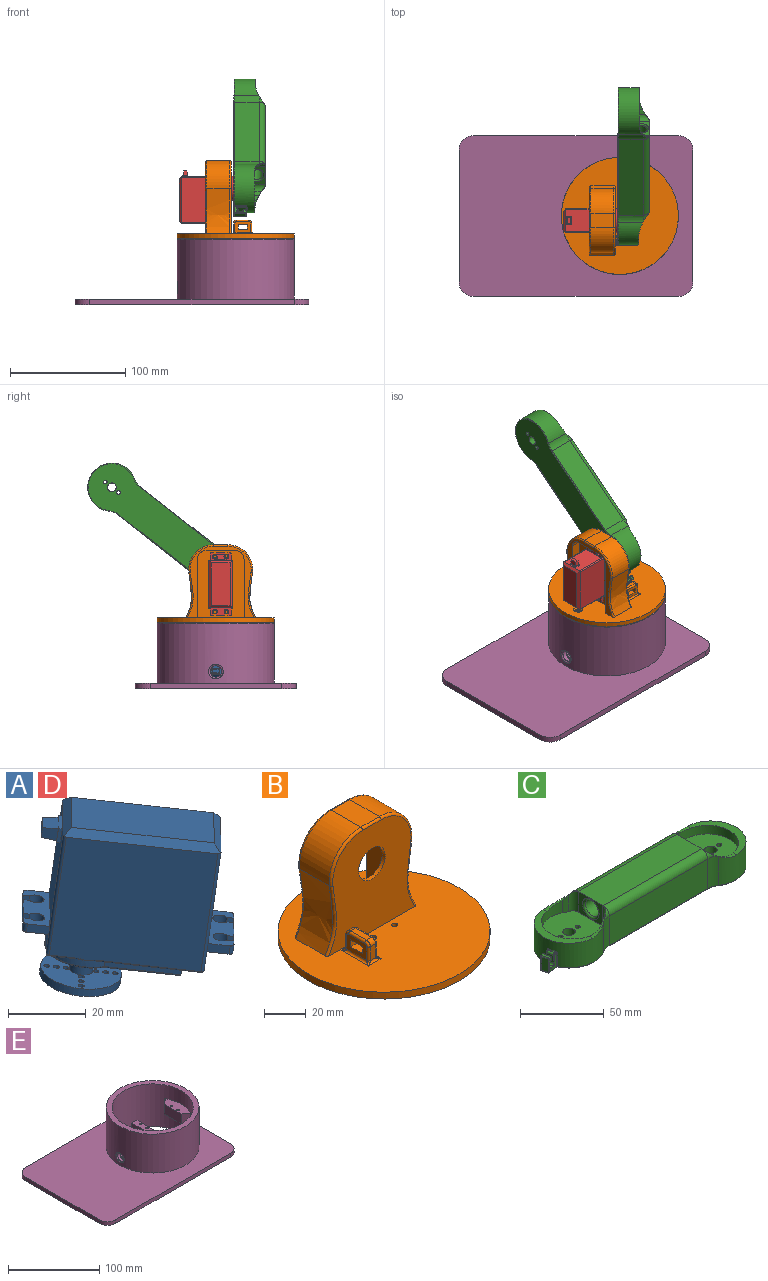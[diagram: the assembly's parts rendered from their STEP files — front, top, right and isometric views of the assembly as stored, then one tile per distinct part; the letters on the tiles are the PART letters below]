
ASSEMBLY  parts=5 mates=7
PART A: 116 faces, bbox 51.5x51x50.8 mm
  f0: cylinder r=0.75mm len=2.43mm, axis (-0.18,0,-0.98), area 10.4mm2, adj f111,f112
  f1: cylinder r=0.75mm len=2.43mm, axis (-0.18,0,-0.98), area 10.4mm2, adj f111,f112
  f2: cylinder r=0.75mm len=2.43mm, axis (-0.18,0,-0.98), area 10.4mm2, adj f111,f112
  f3: cylinder r=0.75mm len=2.43mm, axis (-0.18,0,-0.98), area 10.4mm2, adj f111,f112
  f4: cylinder r=0.75mm len=2.43mm, axis (-0.18,0,-0.98), area 10.4mm2, adj f111,f112
  f5: cylinder r=0.75mm len=2.43mm, axis (-0.18,0,-0.98), area 10.4mm2, adj f111,f112
  f6: cylinder r=0.75mm len=2.43mm, axis (-0.18,0,-0.98), area 10.4mm2, adj f111,f112
  f7: cylinder r=0.75mm len=2.43mm, axis (-0.18,0,-0.98), area 10.4mm2, adj f111,f112
  f8: cylinder r=0.75mm len=2.43mm, axis (-0.18,0,-0.98), area 10.4mm2, adj f111,f112
  f9: cylinder r=0.75mm len=2.43mm, axis (-0.18,0,-0.98), area 10.4mm2, adj f111,f112
  f10: cylinder r=0.75mm len=2.43mm, axis (-0.18,0,-0.98), area 10.4mm2, adj f111,f112
  f11: cylinder r=0.75mm len=2.43mm, axis (-0.18,0,-0.98), area 10.4mm2, adj f111,f112
  f12: cylinder r=10.5mm len=21.06mm, axis (0.18,0,0.98), area 145.1mm2, adj f111,f112
  f13: torus R=9.85mm, axis (-0.18,0,-0.98), area 26.7mm2, adj f21,f47,f82,f83
  f14: cylinder r=2.1mm len=4.56mm, axis (-0.18,0,-0.98), area 25.2mm2, adj f28,f29,f76,f77
  f15: cylinder r=2.1mm len=4.56mm, axis (-0.18,0,-0.98), area 25.2mm2, adj f27,f29,f74,f75
  f16: cylinder r=2.1mm len=4.56mm, axis (-0.18,0,-0.98), area 25.2mm2, adj f31,f33,f64,f65
  f17: cylinder r=2.1mm len=4.56mm, axis (-0.18,0,-0.98), area 25.2mm2, adj f32,f33,f62,f63
  f18: cylinder r=3mm len=6.62mm, axis (0.18,0,0.98), area 75.4mm2, adj f49,f111
  f19: cylinder r=5.35mm len=10.7mm, axis (0.18,0,0.98), area 20.2mm2, adj f48,f49
  f20: cylinder r=6.5mm len=13.02mm, axis (0.18,0,0.98), area 53.1mm2, adj f47,f48
  f21: cylinder r=10.25mm len=20.17mm, axis (0.18,0,0.98), area 81.6mm2, adj f13,f37,f38,f39,f45,f46,f85,f87
  f22: plane 5.62x5.02mm, normal (-0.7,0.71,0.13), area 7.3mm2, adj f102,f103,f104,f105,f106,f107,f108,f109
  f23: plane 36.52x19.42mm, normal (-0.7,0.71,0.13), area 579.5mm2, adj f31,f32,f33,f54,f55,f56,f59,f60
  f24: plane 5.65x5.3mm, normal (0.7,-0.71,-0.13), area 18mm2, adj f27,f28,f29,f74,f77,f80
  f25: plane 5x4.81mm, normal (0.7,0.71,-0.13), area 5.1mm2, adj f27,f40,f80
  f26: plane 5x4.81mm, normal (-0.7,-0.71,0.13), area 5.1mm2, adj f28,f40,f80
  f27: plane 11x10.41mm, normal (-0.18,0,-0.98), area 42.1mm2, adj f15,f24,f25,f40,f72,f73,f74,f75
  f28: plane 10.82x10.58mm, normal (-0.18,0,-0.98), area 42.1mm2, adj f14,f24,f26,f30,f40,f71,f76,f77
  f29: plane 17.48x17.19mm, normal (0.18,0,0.98), area 91mm2, adj f14,f15,f24,f30,f40,f71,f72,f73
  f30: plane 2.61x1.82mm, normal (0.7,-0.71,-0.13), area 4.8mm2, adj f28,f29,f76,f79
  f31: plane 11x10.41mm, normal (-0.18,0,-0.98), area 42.1mm2, adj f16,f23,f34,f59,f61,f64,f65,f67
  f32: plane 10.82x10.58mm, normal (-0.18,0,-0.98), area 42.1mm2, adj f17,f23,f34,f35,f60,f62,f63,f66
  f33: plane 17.48x17.19mm, normal (0.18,0,0.98), area 91mm2, adj f16,f17,f23,f34,f35,f59,f60,f61
  f34: plane 5.65x5.3mm, normal (-0.7,0.71,0.13), area 18mm2, adj f31,f32,f33,f63,f64,f70
  f35: plane 2.61x1.82mm, normal (-0.7,0.71,0.13), area 4.8mm2, adj f32,f33,f62,f66
  f36: cylinder r=3.32mm len=4.53mm, axis (0.18,0,0.98), area 9.6mm2, adj f37,f44,f81
  f37: plane 33.22x32.68mm, normal (-0.18,0,-0.98), area 137.4mm2, adj f21,f36,f44,f45,f46,f86,f88,f89
  f38: plane 9.76x4.79mm, normal (-0.18,0,-0.98), area 16mm2, adj f21,f93,f94,f96
  f39: plane 9.92x4.72mm, normal (-0.18,0,-0.98), area 16mm2, adj f21,f98,f99,f101
  f40: plane 36.43x19.34mm, normal (0.7,-0.71,-0.13), area 608mm2, adj f25,f26,f27,f28,f29,f51,f57,f58
  f41: plane 39.21x33.78mm, normal (-0.7,-0.71,0.13), area 1364.1mm2, adj f52,f55,f57,f85,f86,f97,f98
  f42: plane 39.11x33.68mm, normal (0.7,0.71,-0.13), area 1364.1mm2, adj f53,f56,f58,f87,f89,f95,f96
  f43: plane 37.83x37.22mm, normal (0.18,0,0.98), area 610.5mm2, adj f51,f52,f53,f54
  f44: plane 12.79x12.65mm, normal (0.7,-0.71,-0.13), area 23.7mm2, adj f36,f37,f45,f46,f50,f81,f84
  f45: plane 14.2x14.09mm, normal (-0.7,-0.71,0.13), area 37.9mm2, adj f21,f37,f44,f83
  f46: plane 14.2x14.09mm, normal (0.7,0.71,-0.13), area 37.9mm2, adj f21,f37,f44,f82
  f47: plane 33.27x32.74mm, normal (-0.18,0,-0.98), area 446.8mm2, adj f13,f20,f82,f83,f84
  f48: plane 13x12.79mm, normal (-0.18,0,-0.98), area 42.8mm2, adj f19,f20
  f49: plane 10.7x10.53mm, normal (-0.18,0,-0.98), area 61.6mm2, adj f18,f19
  f50: plane 3.65x3.59mm, normal (-0.18,0,-0.98), area 5.1mm2, adj f44,f81
  f51: plane 14.28x14.05mm, normal (0.62,-0.5,0.61), area 52.1mm2, adj f40,f43,f52,f53,f57,f58
  f52: plane 28.77x28.63mm, normal (-0.37,-0.5,0.79), area 110.1mm2, adj f41,f43,f51,f54,f55,f57
  f53: plane 28.77x28.31mm, normal (0.62,0.5,0.61), area 110.1mm2, adj f42,f43,f51,f54,f56,f58
  f54: plane 14.37x14.28mm, normal (-0.37,0.5,0.79), area 52.1mm2, adj f23,f43,f52,f53,f55,f56
  f55: cylinder r=0.8mm len=34.32mm, axis (0.18,0,0.98), area 43.6mm2, adj f23,f41,f52,f54,f99
  f56: cylinder r=0.8mm len=34.48mm, axis (0.18,0,0.98), area 43.6mm2, adj f23,f42,f53,f54,f94
  f57: cylinder r=0.8mm len=34.48mm, axis (0.18,0,0.98), area 43.6mm2, adj f40,f41,f51,f52,f88
  f58: cylinder r=0.8mm len=34.32mm, axis (0.18,0,0.98), area 43.6mm2, adj f40,f42,f51,f53,f91
  f59: plane 4.46x4.1mm, normal (-0.7,-0.71,0.13), area 13.9mm2, adj f23,f31,f33,f67
  f60: plane 4.46x4.1mm, normal (0.7,0.71,-0.13), area 13.9mm2, adj f23,f32,f33,f66
  f61: plane 2.61x1.82mm, normal (-0.7,0.71,0.13), area 4.8mm2, adj f31,f33,f65,f67
  f62: plane 2.57x1.55mm, normal (-0.7,-0.71,0.13), area 3.9mm2, adj f17,f32,f33,f35
  f63: plane 2.57x1.55mm, normal (0.7,0.71,-0.13), area 3.9mm2, adj f17,f32,f33,f34
  f64: plane 2.57x1.55mm, normal (-0.7,-0.71,0.13), area 3.9mm2, adj f16,f31,f33,f34
  f65: plane 2.57x1.55mm, normal (0.7,0.71,-0.13), area 3.9mm2, adj f16,f31,f33,f61
  f66: cylinder r=1mm len=2.61mm, axis (0.18,0,0.98), area 3.8mm2, adj f32,f33,f35,f60
  f67: cylinder r=1mm len=2.41mm, axis (-0.18,0,-0.98), area 3.8mm2, adj f31,f33,f59,f61
  f68: plane 4.81x4.73mm, normal (-0.7,-0.71,0.13), area 5.1mm2, adj f23,f31,f70
  f69: plane 4.81x4.73mm, normal (0.7,0.71,-0.13), area 5.1mm2, adj f23,f32,f70
  f70: plane 5.52x5.16mm, normal (-0.32,0.15,-0.93), area 7mm2, adj f23,f34,f68,f69
  f71: plane 4.46x4.1mm, normal (-0.7,-0.71,0.13), area 13.9mm2, adj f28,f29,f40,f79
  f72: plane 4.46x4.1mm, normal (0.7,0.71,-0.13), area 13.9mm2, adj f27,f29,f40,f78
  f73: plane 2.61x1.82mm, normal (0.7,-0.71,-0.13), area 4.8mm2, adj f27,f29,f75,f78
  f74: plane 2.57x1.55mm, normal (0.7,0.71,-0.13), area 3.9mm2, adj f15,f24,f27,f29
  f75: plane 2.57x1.55mm, normal (-0.7,-0.71,0.13), area 3.9mm2, adj f15,f27,f29,f73
  f76: plane 2.57x1.55mm, normal (0.7,0.71,-0.13), area 3.9mm2, adj f14,f28,f29,f30
  f77: plane 2.57x1.55mm, normal (-0.7,-0.71,0.13), area 3.9mm2, adj f14,f24,f28,f29
  f78: cylinder r=1mm len=2.41mm, axis (-0.18,0,-0.98), area 3.8mm2, adj f27,f29,f72,f73
  f79: cylinder r=1mm len=2.61mm, axis (0.18,0,0.98), area 3.8mm2, adj f28,f29,f30,f71
  f80: plane 5.69x5.52mm, normal (-0.02,-0.15,-0.99), area 7mm2, adj f24,f25,f26,f40
  f81: torus R=2.92mm, axis (-0.18,0,-0.98), area 4.3mm2, adj f36,f44,f50
  f82: cylinder r=0.4mm len=14.45mm, axis (-0.7,0.71,0.13), area 12.4mm2, adj f13,f46,f47,f84
  f83: cylinder r=0.4mm len=14.45mm, axis (0.7,-0.71,-0.13), area 12.4mm2, adj f13,f45,f47,f84
  f84: cylinder r=0.4mm len=12.83mm, axis (0.7,0.71,-0.13), area 10.9mm2, adj f44,f47,f82,f83
  f85: bspline ~2.25x2.01mm, area 0.6mm2, adj f21,f41,f86
  f86: cylinder r=0.4mm len=19.46mm, axis (-0.7,0.71,0.13), area 17mm2, adj f37,f41,f85,f88
  f87: bspline ~2.29x2.04mm, area 0.6mm2, adj f21,f42,f89
  f88: torus R=0.4mm, axis (0.18,0,0.98), area 0.6mm2, adj f37,f57,f86,f90
  f89: cylinder r=0.4mm len=19.46mm, axis (0.7,-0.71,-0.13), area 17mm2, adj f37,f42,f87,f91
  f90: cylinder r=0.4mm len=13.65mm, axis (-0.7,-0.71,0.13), area 11.9mm2, adj f37,f40,f88,f91
  f91: torus R=0.4mm, axis (0.18,0,0.98), area 0.6mm2, adj f37,f58,f89,f90
  f92: bspline ~2.25x2.01mm, area 0.6mm2, adj f21,f23,f93
  f93: cylinder r=0.4mm len=4.96mm, axis (0.7,0.71,-0.13), area 4.2mm2, adj f23,f38,f92,f94
  f94: torus R=0.4mm, axis (0.18,0,0.98), area 0.6mm2, adj f38,f56,f93,f96
  f95: bspline ~2.25x2.01mm, area 0.6mm2, adj f21,f42,f96
  f96: cylinder r=0.4mm len=4.96mm, axis (0.7,-0.71,-0.13), area 4.2mm2, adj f38,f42,f94,f95
  f97: bspline ~2.29x1.97mm, area 0.6mm2, adj f21,f41,f98
  f98: cylinder r=0.4mm len=4.96mm, axis (-0.7,0.71,0.13), area 4.2mm2, adj f39,f41,f97,f99
  f99: torus R=0.4mm, axis (0.18,0,0.98), area 0.6mm2, adj f39,f55,f98,f101
  f100: bspline ~2.29x1.97mm, area 0.6mm2, adj f21,f23,f101
  f101: cylinder r=0.4mm len=4.96mm, axis (0.7,0.71,-0.13), area 4.2mm2, adj f23,f39,f99,f100
  f102: plane 4.26x1.45mm, normal (0.7,0.71,-0.13), area 4.2mm2, adj f22,f23,f103,f105
  f103: plane 5.66x5.57mm, normal (-0.18,0,-0.98), area 7mm2, adj f22,f23,f102,f104
  f104: plane 4.26x1.45mm, normal (-0.7,-0.71,0.13), area 4.2mm2, adj f22,f23,f103,f105
  f105: plane 5.66x5.57mm, normal (0.18,0,0.98), area 7mm2, adj f22,f23,f102,f104
  f106: plane 3.65x3.59mm, normal (0.63,0.77,-0.11), area 12.6mm2, adj f22,f107,f109,f110
  f107: plane 7.04x6.86mm, normal (-0.24,0.06,-0.97), area 23.9mm2, adj f22,f106,f108,f110
  f108: plane 3.56x3.1mm, normal (-0.75,-0.64,0.14), area 12.6mm2, adj f22,f107,f109,f110
  f109: plane 7.04x6.99mm, normal (0.12,0.06,0.99), area 23.9mm2, adj f22,f106,f108,f110
  f110: plane 4.4x3.96mm, normal (-0.7,0.71,0.13), area 15.7mm2, adj f106,f107,f108,f109
  f111: plane 21x20.66mm, normal (0.18,0,0.98), area 296.9mm2, adj f0,f1,f2,f3,f4,f5,f6,f7
  f112: plane 21x20.66mm, normal (-0.18,0,-0.98), area 325.2mm2, adj f0,f1,f2,f3,f4,f5,f6,f7
  f113: cylinder r=1.25mm len=4.38mm, axis (-0.18,0,-0.98), area 31.4mm2, adj f114,f115
  f114: plane 2.5x2.46mm, normal (-0.18,0,-0.98), area 4.9mm2, adj f113
  f115: plane 2.5x2.46mm, normal (0.18,0,0.98), area 4.9mm2, adj f113
PART B: 76 faces, bbox 101.9x101.9x69.5 mm
  f0: plane 13.46x9.46mm, normal (1,0,0), area 94.6mm2, adj f44,f45,f46,f47,f49,f63,f64,f65
  f1: plane 13.46x9.46mm, normal (-1,0,0), area 94.6mm2, adj f44,f45,f46,f47,f50,f70,f71,f72
  f2: plane 62.24x57.86mm, normal (0,1,0), area 673.2mm2, adj f6,f13,f14,f15,f16,f17,f57,f58
  f3: plane 62.24x57.86mm, normal (0,-1,0), area 2768mm2, adj f6,f23,f52,f53,f54,f55,f56
  f4: plane 19.96x12.41mm, normal (0,0,1), area 247.6mm2, adj f34,f35,f54,f60
  f5: plane 58.42x40.64mm, normal (0,1,0), area 1458.6mm2, adj f6,f13,f14,f15,f16,f17,f18,f19
  f6: plane 101.86x101.86mm, normal (0,0,1), area 6871.9mm2, adj f2,f3,f5,f8,f11,f12,f13,f17
  f7: plane 101.6x101.6mm, normal (0,0,-1), area 8004.4mm2, adj f8,f9,f11,f12,f38
  f8: cylinder r=50.8mm len=101.6mm, axis (0,0,-1), area 1276.7mm2, adj f6,f7
  f9: cylinder r=3.75mm len=7.5mm, axis (0,0,-1), area 35.3mm2, adj f7,f10
  f10: plane 7.5x7.5mm, normal (0,0,-1), area 44.2mm2, adj f9
  f11: cylinder r=1.5mm len=4mm, axis (0,0,-1), area 37.7mm2, adj f6,f7
  f12: cylinder r=1.5mm len=4mm, axis (0,0,-1), area 37.7mm2, adj f6,f7
  f13: plane 50.8x8.5mm, normal (1,0,0), area 431.8mm2, adj f2,f5,f6,f14
  f14: cylinder r=7.62mm len=8.5mm, axis (0,1,0), area 101.7mm2, adj f2,f5,f13,f15
  f15: plane 25.4x8.5mm, normal (0,0,-1), area 215.9mm2, adj f2,f5,f14,f16
  f16: cylinder r=7.62mm len=8.5mm, axis (0,1,0), area 101.7mm2, adj f2,f5,f15,f17
  f17: plane 50.8x8.5mm, normal (-1,0,0), area 431.8mm2, adj f2,f5,f6,f16
  f18: plane 21x12mm, normal (0,0,1), area 252mm2, adj f5,f19,f21,f22
  f19: plane 41.4x12mm, normal (1,0,0), area 496.8mm2, adj f5,f18,f20,f22
  f20: plane 21x12mm, normal (0,0,-1), area 252mm2, adj f5,f19,f21,f22
  f21: plane 41.4x12mm, normal (-1,0,0), area 496.8mm2, adj f5,f18,f20,f22
  f22: plane 41.4x21mm, normal (0,1,0), area 615mm2, adj f18,f19,f20,f21,f23
  f23: cylinder r=9mm len=18mm, axis (0,1,0), area 113.1mm2, adj f3,f22
  f24: cylinder r=1.3mm len=7.5mm, axis (0,1,0), area 61.3mm2, adj f5,f25
  f25: plane 2.6x2.6mm, normal (0,1,0), area 5.3mm2, adj f24
  f26: cylinder r=1.3mm len=7.5mm, axis (0,1,0), area 61.3mm2, adj f5,f27
  f27: plane 2.6x2.6mm, normal (0,1,0), area 5.3mm2, adj f26
  f28: cylinder r=1.3mm len=7.5mm, axis (0,1,0), area 61.3mm2, adj f5,f29
  f29: plane 2.6x2.6mm, normal (0,1,0), area 5.3mm2, adj f28
  f30: cylinder r=1.3mm len=7.5mm, axis (0,1,0), area 61.3mm2, adj f5,f31
  f31: plane 2.6x2.6mm, normal (0,1,0), area 5.3mm2, adj f30
  f32: extruded ~39.77x19.96mm, area 815.7mm2, adj f6,f35,f52,f57
  f33: extruded ~39.77x19.96mm, area 815.7mm2, adj f6,f34,f55,f59
  f34: cylinder r=21.59mm len=23.74mm, axis (0,1,0), area 719.8mm2, adj f4,f33,f56,f61
  f35: cylinder r=21.59mm len=23.74mm, axis (0,1,0), area 719.8mm2, adj f4,f32,f53,f58
  f36: cylinder r=2.5mm len=5mm, axis (0,0,1), area 22.9mm2, adj f37,f38
  f37: torus R=3.77mm, axis (0,0,1), area 37.1mm2, adj f6,f36
  f38: torus R=3.77mm, axis (0,0,1), area 37.1mm2, adj f7,f36
  f39: plane 8.19x3.46mm, normal (0,-1,0), area 28.3mm2, adj f43,f48,f67,f70
  f40: plane 8.19x3.46mm, normal (0,1,0), area 28.3mm2, adj f42,f51,f63,f74
  f41: plane 10.92x3.46mm, normal (0,0,1), area 37.8mm2, adj f42,f43,f65,f72
  f42: cylinder r=2.54mm len=3.46mm, axis (1,0,0), area 13.8mm2, adj f40,f41,f64,f73
  f43: cylinder r=2.54mm len=3.46mm, axis (-1,0,0), area 13.8mm2, adj f39,f41,f66,f71
  f44: plane 8x6mm, normal (0,0,1), area 48mm2, adj f0,f1,f45,f47
  f45: plane 6x4mm, normal (0,-1,0), area 24mm2, adj f0,f1,f44,f46
  f46: plane 8x6mm, normal (0,0,-1), area 48mm2, adj f0,f1,f45,f47
  f47: plane 6x4mm, normal (0,1,0), area 24mm2, adj f0,f1,f44,f46
  f48: cylinder r=1.27mm len=8.54mm, axis (1,0,0), area 12mm2, adj f6,f39,f68,f69
  f49: cylinder r=1.27mm len=18.54mm, axis (0,1,0), area 31.9mm2, adj f0,f6,f62,f68
  f50: cylinder r=1.27mm len=18.54mm, axis (0,-1,0), area 31.9mm2, adj f1,f6,f69,f75
  f51: cylinder r=1.27mm len=8.54mm, axis (-1,0,0), area 12mm2, adj f6,f40,f62,f75
  f52: bspline ~44.89x7.82mm, area 81.4mm2, adj f3,f6,f32,f53
  f53: torus R=20.32mm, axis (0,1,0), area 70.4mm2, adj f3,f35,f52,f54
  f54: cylinder r=1.27mm len=12.41mm, axis (-1,0,0), area 24.7mm2, adj f3,f4,f53,f56
  f55: bspline ~44.89x7.82mm, area 81.4mm2, adj f3,f6,f33,f56
  f56: torus R=20.32mm, axis (0,1,0), area 70.4mm2, adj f3,f34,f54,f55
  f57: bspline ~44.89x7.82mm, area 81.4mm2, adj f2,f6,f32,f58
  f58: torus R=20.32mm, axis (0,1,0), area 70.4mm2, adj f2,f35,f57,f60
  f59: bspline ~44.89x7.82mm, area 81.4mm2, adj f2,f6,f33,f61
  f60: cylinder r=1.27mm len=12.41mm, axis (1,0,0), area 24.7mm2, adj f2,f4,f58,f61
  f61: torus R=20.32mm, axis (0,1,0), area 70.4mm2, adj f2,f34,f59,f60
  f62: bspline ~2.54x2.54mm, area 1.7mm2, adj f49,f51,f63
  f63: cylinder r=1.27mm len=8.19mm, axis (0,0,-1), area 16.3mm2, adj f0,f40,f62,f64
  f64: torus R=1.27mm, axis (-1,0,0), area 6.5mm2, adj f0,f42,f63,f65
  f65: cylinder r=1.27mm len=10.92mm, axis (0,-1,0), area 21.8mm2, adj f0,f41,f64,f66
  f66: torus R=1.27mm, axis (-1,0,0), area 6.5mm2, adj f0,f43,f65,f67
  f67: cylinder r=1.27mm len=8.19mm, axis (0,0,1), area 16.3mm2, adj f0,f39,f66,f68
  f68: bspline ~2.54x2.54mm, area 1.7mm2, adj f48,f49,f67
  f69: bspline ~2.54x2.54mm, area 1.7mm2, adj f48,f50,f70
  f70: cylinder r=1.27mm len=8.19mm, axis (0,0,-1), area 16.3mm2, adj f1,f39,f69,f71
  f71: torus R=1.27mm, axis (-1,0,0), area 6.5mm2, adj f1,f43,f70,f72
  f72: cylinder r=1.27mm len=10.92mm, axis (0,1,0), area 21.8mm2, adj f1,f41,f71,f73
  f73: torus R=1.27mm, axis (-1,0,0), area 6.5mm2, adj f1,f42,f72,f74
  f74: cylinder r=1.27mm len=8.19mm, axis (0,0,1), area 16.3mm2, adj f1,f40,f73,f75
  f75: bspline ~2.54x2.54mm, area 1.7mm2, adj f50,f51,f74
PART C: 113 faces, bbox 171.4x45.5x28.2 mm
  f0: plane 9.98x6.97mm, normal (-0.19,0.98,0), area 32.9mm2, adj f62,f65,f66,f69,f70,f73,f74,f77
  f1: plane 4.91x1.58mm, normal (0,0,1), area 1.7mm2, adj f55,f89,f90,f91
  f2: cylinder r=21mm len=42mm, axis (0,0,-1), area 1562mm2, adj f6,f12,f30,f31,f32,f90,f95,f96
  f3: plane 37.08x33.94mm, normal (0,0,1), area 987.5mm2, adj f4,f16,f17,f18,f27,f28,f29,f43
  f4: plane 20.33x15.24mm, normal (-1,0,0), area 156.6mm2, adj f3,f21,f43,f44,f45
  f5: plane 37.08x34.02mm, normal (0,0,1), area 989.7mm2, adj f13,f14,f15,f20,f23,f24,f25,f41
  f6: cylinder r=12.7mm len=21.65mm, axis (0,0,-1), area 158.1mm2, adj f2,f7,f31,f35,f106
  f7: plane 83.29x21.65mm, normal (0,-1,0), area 1803.4mm2, adj f6,f8,f36,f108
  f8: cylinder r=12.7mm len=21.65mm, axis (0,0,-1), area 158.1mm2, adj f7,f9,f33,f37,f110
  f9: cylinder r=21mm len=42mm, axis (0,0,-1), area 1637.3mm2, adj f8,f10,f26,f33,f34,f112
  f10: cylinder r=12.7mm len=21.65mm, axis (0,0,-1), area 158.1mm2, adj f9,f11,f34,f40,f111
  f11: plane 83.29x21.65mm, normal (0,1,0), area 1803.4mm2, adj f10,f12,f39,f109
  f12: cylinder r=12.7mm len=21.65mm, axis (0,0,-1), area 158.1mm2, adj f2,f11,f32,f38,f107
  f13: cylinder r=3.75mm len=12mm, axis (0,0,-1), area 282.7mm2, adj f5,f19
  f14: cylinder r=1.5mm len=12mm, axis (0,0,-1), area 113.1mm2, adj f5,f19
  f15: cylinder r=1.5mm len=12mm, axis (0,0,-1), area 113.1mm2, adj f5,f19
  f16: cylinder r=3.75mm len=12mm, axis (0,0,-1), area 282.7mm2, adj f3,f19
  f17: cylinder r=1.5mm len=12mm, axis (0,0,-1), area 113.1mm2, adj f3,f19
  f18: cylinder r=1.5mm len=12mm, axis (0,0,-1), area 113.1mm2, adj f3,f19
  f19: plane 168.64x40.98mm, normal (0,0,-1), area 5070.5mm2, adj f13,f14,f15,f16,f17,f18,f93,f98
  f20: plane 20.31x15.24mm, normal (1,0,0), area 156.2mm2, adj f5,f21,f41,f42,f46
  f21: plane 83.29x20.97mm, normal (0,0,1), area 1746.1mm2, adj f4,f20,f31,f32,f33,f34,f36,f39
  f22: cylinder r=5.71mm len=80.75mm, axis (1,0,0), area 2899.6mm2, adj f45,f46
  f23: cylinder r=13.72mm len=11.7mm, axis (0,0,-1), area 43.1mm2, adj f5,f24,f34,f41
  f24: cylinder r=18.54mm len=37.08mm, axis (0,0,-1), area 498.6mm2, adj f5,f23,f25,f26,f33,f34
  f25: cylinder r=13.72mm len=11.68mm, axis (0,0,-1), area 42.5mm2, adj f5,f24,f33,f42
  f26: plane 41.96x20.05mm, normal (0,0,1), area 253.9mm2, adj f9,f24,f33,f34
  f27: cylinder r=13.72mm len=11.7mm, axis (0,0,-1), area 43.1mm2, adj f3,f28,f31,f44
  f28: cylinder r=18.54mm len=37.08mm, axis (0,0,-1), area 497.5mm2, adj f3,f27,f29,f30,f31,f32
  f29: cylinder r=13.72mm len=11.7mm, axis (0,0,-1), area 43.1mm2, adj f3,f28,f32,f43
  f30: plane 41.96x20.05mm, normal (0,0,1), area 256.6mm2, adj f2,f28,f31,f32
  f31: cylinder r=25.4mm len=19.3mm, axis (0,-1,0), area 31.9mm2, adj f2,f6,f21,f27,f28,f30,f35,f44
  f32: cylinder r=25.4mm len=19.3mm, axis (0,-1,0), area 31.9mm2, adj f2,f12,f21,f28,f29,f30,f38,f43
  f33: cylinder r=25.4mm len=19.3mm, axis (0,-1,0), area 32.8mm2, adj f8,f9,f21,f24,f25,f26,f37,f42
  f34: cylinder r=25.4mm len=19.3mm, axis (0,-1,0), area 31.6mm2, adj f9,f10,f21,f23,f24,f26,f40,f41
  f35: torus R=17.78mm, axis (0,0,1), area 15.4mm2, adj f6,f31,f36
  f36: cylinder r=5.08mm len=83.29mm, axis (-1,0,0), area 664.6mm2, adj f7,f21,f35,f37
  f37: torus R=17.78mm, axis (0,0,1), area 15.4mm2, adj f8,f33,f36
  f38: torus R=17.78mm, axis (0,0,1), area 15.4mm2, adj f12,f32,f39
  f39: cylinder r=5.08mm len=83.29mm, axis (1,0,0), area 664.6mm2, adj f11,f21,f38,f40
  f40: torus R=17.78mm, axis (0,0,1), area 15.4mm2, adj f10,f34,f39
  f41: cylinder r=5.08mm len=15.24mm, axis (0,0,-1), area 91.5mm2, adj f5,f20,f23,f34
  f42: cylinder r=5.08mm len=15.24mm, axis (0,0,-1), area 91.9mm2, adj f5,f20,f25,f33
  f43: cylinder r=5.08mm len=15.24mm, axis (0,0,-1), area 91.5mm2, adj f3,f4,f29,f32
  f44: cylinder r=5.08mm len=15.24mm, axis (0,0,-1), area 91.5mm2, adj f3,f4,f27,f31
  f45: torus R=6.99mm, axis (1,0,0), area 77.4mm2, adj f4,f22
  f46: torus R=6.99mm, axis (1,0,0), area 77.4mm2, adj f20,f22
  f47: plane 9.98x7.13mm, normal (0.19,-0.98,0), area 34.5mm2, adj f61,f63,f64,f67,f68,f71,f72,f75
  f48: plane 9.98x4.79mm, normal (-0.96,-0.27,0), area 49.7mm2, adj f83,f88,f92,f93
  f49: plane 5.18x2.95mm, normal (0,0,1), area 9.1mm2, adj f59,f79,f82,f83
  f50: plane 5.21x2.7mm, normal (0,0,1), area 8.8mm2, adj f56,f57,f72,f73
  f51: plane 4.87x3.56mm, normal (0.98,0.19,0), area 17.6mm2, adj f57,f60,f64,f65
  f52: plane 4.98x1.5mm, normal (0,0,-1), area 2.8mm2, adj f58,f60,f63,f66
  f53: plane 5.59x4.87mm, normal (-0.98,-0.19,0), area 27.7mm2, adj f55,f56,f80,f81
  f54: plane 4.87x0.95mm, normal (0.98,0.19,0), area 2.5mm2, adj f58,f59,f71,f74
  f55: cylinder r=1.27mm len=5.11mm, axis (-0.19,0.98,0), area 9.9mm2, adj f1,f53,f85,f86
  f56: cylinder r=1.27mm len=5.11mm, axis (0.19,-0.98,0), area 9.9mm2, adj f50,f53,f76,f77
  f57: cylinder r=1.27mm len=5.11mm, axis (0.19,-0.98,0), area 9.9mm2, adj f50,f51,f68,f69
  f58: cylinder r=1.27mm len=5.11mm, axis (-0.19,0.98,0), area 9.9mm2, adj f52,f54,f67,f70
  f59: cylinder r=1.27mm len=5.11mm, axis (-0.19,0.98,0), area 9.9mm2, adj f49,f54,f75,f78
  f60: cylinder r=0.25mm len=4.92mm, axis (0.19,-0.98,0), area 2mm2, adj f51,f52,f61,f62
  f61: torus R=0.76mm, axis (-0.19,0.98,0), area 0.5mm2, adj f47,f60,f63,f64
  f62: torus R=0.76mm, axis (0.19,-0.98,0), area 0.5mm2, adj f0,f60,f65,f66
  f63: cylinder r=0.51mm len=0.65mm, axis (0.98,0.19,0), area 0.4mm2, adj f47,f52,f61,f67
  f64: cylinder r=0.51mm len=3.56mm, axis (0,0,1), area 2.8mm2, adj f47,f51,f61,f68
  f65: cylinder r=0.51mm len=3.56mm, axis (0,0,1), area 2.8mm2, adj f0,f51,f62,f69
  f66: cylinder r=0.51mm len=0.65mm, axis (0.98,0.19,0), area 0.4mm2, adj f0,f52,f62,f70
  f67: torus R=0.76mm, axis (-0.19,0.98,0), area 1.4mm2, adj f47,f58,f63,f71
  f68: torus R=1.78mm, axis (-0.19,0.98,0), area 1.8mm2, adj f47,f57,f64,f72
  f69: torus R=1.78mm, axis (0.19,-0.98,0), area 1.8mm2, adj f0,f57,f65,f73
  f70: torus R=0.76mm, axis (0.19,-0.98,0), area 1.4mm2, adj f0,f58,f66,f74
  f71: cylinder r=0.51mm len=0.6mm, axis (0,0,1), area 0.4mm2, adj f47,f54,f67,f75
  f72: cylinder r=0.51mm len=1.84mm, axis (-0.98,-0.19,0), area 1.4mm2, adj f47,f50,f68,f76
  f73: cylinder r=0.51mm len=1.84mm, axis (-0.98,-0.19,0), area 1.4mm2, adj f0,f50,f69,f77
  f74: cylinder r=0.51mm len=0.6mm, axis (0,0,1), area 0.4mm2, adj f0,f54,f70,f78
  f75: torus R=0.76mm, axis (-0.19,0.98,0), area 1.4mm2, adj f47,f59,f71,f79
  f76: torus R=1.78mm, axis (-0.19,0.98,0), area 1.8mm2, adj f47,f56,f72,f80
  f77: torus R=1.78mm, axis (0.19,-0.98,0), area 1.8mm2, adj f0,f56,f73,f81
  f78: torus R=0.76mm, axis (0.19,-0.98,0), area 1.4mm2, adj f0,f59,f74,f82
  f79: cylinder r=0.51mm len=1.68mm, axis (0.98,0.19,0), area 1.3mm2, adj f47,f49,f75,f84
  f80: cylinder r=0.51mm len=5.59mm, axis (0,0,-1), area 4.5mm2, adj f47,f53,f76,f85
  f81: cylinder r=0.51mm len=5.59mm, axis (0,0,-1), area 4.5mm2, adj f0,f53,f77,f86
  f82: cylinder r=0.51mm len=2.1mm, axis (-0.98,-0.19,0), area 1.6mm2, adj f0,f49,f78,f87
  f83: cylinder r=0.51mm len=4.93mm, axis (0.27,-0.96,0), area 4mm2, adj f48,f49,f84,f87
  f84: sphere r=0.51mm, area 0.4mm2, adj f79,f83,f88
  f85: torus R=0.76mm, axis (-0.19,0.98,0), area 1.4mm2, adj f47,f55,f80,f89
  f86: torus R=0.76mm, axis (0.19,-0.98,0), area 1.4mm2, adj f0,f55,f81,f91
  f87: sphere r=0.51mm, area 0.4mm2, adj f82,f83,f92
  f88: cylinder r=0.51mm len=9.98mm, axis (0,0,-1), area 7.5mm2, adj f47,f48,f84,f94
  f89: cylinder r=0.51mm len=0.95mm, axis (0.98,0.19,0), area 0.6mm2, adj f1,f47,f85,f95
  f90: torus R=21.51mm, axis (0,0,-1), area 3.9mm2, adj f1,f2,f95,f96
  f91: cylinder r=0.51mm len=0.55mm, axis (-0.98,-0.19,0), area 0.2mm2, adj f0,f1,f86,f96
  f92: cylinder r=0.51mm len=9.98mm, axis (0,0,-1), area 8.4mm2, adj f0,f48,f87,f97
  f93: cylinder r=0.51mm len=4.93mm, axis (0.27,-0.96,0), area 4mm2, adj f19,f48,f94,f97
  f94: sphere r=0.51mm, area 0.4mm2, adj f88,f93,f98
  f95: bspline ~1.21x1.15mm, area 0.8mm2, adj f2,f89,f90,f99
  f96: bspline ~1.24x1.15mm, area 0.8mm2, adj f2,f90,f91,f100
  f97: sphere r=0.51mm, area 0.4mm2, adj f92,f93,f101
  f98: cylinder r=0.51mm len=7.23mm, axis (0.98,0.19,0), area 5.8mm2, adj f19,f47,f94,f102
  f99: cylinder r=0.51mm len=9.98mm, axis (0,0,-1), area 6.7mm2, adj f2,f47,f95,f102
  f100: cylinder r=0.51mm len=9.98mm, axis (0,0,-1), area 7.6mm2, adj f0,f2,f96,f103
  f101: cylinder r=0.51mm len=7.07mm, axis (-0.98,-0.19,0), area 5.7mm2, adj f0,f19,f97,f103
  f102: torus R=1.02mm, axis (0,0,1), area 0.7mm2, adj f19,f98,f99,f104
  f103: torus R=1.02mm, axis (0,0,1), area 0.8mm2, adj f19,f100,f101,f105
  f104: torus R=20.49mm, axis (0,0,1), area 28.3mm2, adj f2,f19,f102,f106
  f105: torus R=20.49mm, axis (0,0,1), area 37.5mm2, adj f2,f19,f103,f107
  f106: torus R=13.21mm, axis (0,0,1), area 5.9mm2, adj f6,f19,f104,f108
  f107: torus R=13.21mm, axis (0,0,1), area 5.9mm2, adj f12,f19,f105,f109
  f108: cylinder r=0.51mm len=83.29mm, axis (1,0,0), area 66.5mm2, adj f7,f19,f106,f110
  f109: cylinder r=0.51mm len=83.29mm, axis (-1,0,0), area 66.5mm2, adj f11,f19,f107,f111
  f110: torus R=13.21mm, axis (0,0,1), area 5.9mm2, adj f8,f19,f108,f112
  f111: torus R=13.21mm, axis (0,0,1), area 5.9mm2, adj f10,f19,f109,f112
  f112: torus R=20.49mm, axis (0,0,1), area 71.3mm2, adj f9,f19,f110,f111
PART D: same geometry as A
PART E: 53 faces, bbox 203.2x139.7x57.1 mm
  f0: cylinder r=44.45mm len=88.9mm, axis (0,0,-1), area 14598.7mm2, adj f2,f3,f14,f22,f37,f44,f49,f50
  f1: cylinder r=50.8mm len=101.6mm, axis (0,0,-1), area 16470.8mm2, adj f13,f14,f43
  f2: plane 42.02x13.25mm, normal (0,0,1), area 399.5mm2, adj f0,f33,f34,f35,f38,f40,f51,f52
  f3: plane 203.2x139.7mm, normal (0,0,-1), area 23058.5mm2, adj f0,f5,f6,f7,f8,f9,f10,f11
  f4: plane 26x8mm, normal (0,0,1), area 197.4mm2, adj f15,f23,f24,f25,f29,f31
  f5: plane 114.3x5.08mm, normal (-1,0,0), area 580.6mm2, adj f3,f6,f12,f13
  f6: cylinder r=12.7mm len=12.7mm, axis (0,0,-1), area 101.3mm2, adj f3,f5,f7,f13
  f7: plane 177.8x5.08mm, normal (0,-1,0), area 903.2mm2, adj f3,f6,f8,f13
  f8: cylinder r=12.7mm len=12.7mm, axis (0,0,-1), area 101.3mm2, adj f3,f7,f9,f13
  f9: plane 114.3x5.08mm, normal (1,0,0), area 580.6mm2, adj f3,f8,f10,f13
  f10: cylinder r=12.7mm len=12.7mm, axis (0,0,-1), area 101.3mm2, adj f3,f9,f11,f13
  f11: plane 177.8x5.08mm, normal (0,1,0), area 903.2mm2, adj f3,f10,f12,f13
  f12: cylinder r=12.7mm len=12.7mm, axis (0,0,-1), area 101.3mm2, adj f3,f5,f11,f13
  f13: plane 203.2x139.7mm, normal (0,0,1), area 20141.3mm2, adj f1,f5,f6,f7,f8,f9,f10,f11
  f14: plane 101.6x101.6mm, normal (0,0,1), area 1900.2mm2, adj f0,f1
  f15: plane 39.08x26mm, normal (1,0,0), area 698.6mm2, adj f3,f4,f16,f21,f22,f23,f25,f26
  f16: plane 18.85x15.82mm, normal (0.64,-0.77,0), area 125mm2, adj f3,f15,f22,f49
  f17: plane 29.82x5.08mm, normal (-1,0,0), area 151.5mm2, adj f3,f22,f45,f48
  f18: plane 5.08x2.78mm, normal (-0.64,-0.77,0), area 18.4mm2, adj f3,f22,f45,f46
  f19: extruded ~37.09x5.55mm, area 199.1mm2, adj f3,f22,f46,f47
  f20: plane 5.08x2.78mm, normal (-0.64,0.77,0), area 18.4mm2, adj f3,f22,f47,f48
  f21: plane 18.85x15.82mm, normal (0.64,0.77,0), area 125mm2, adj f3,f15,f22,f50
  f22: plane 65.25x33.2mm, normal (0,0,1), area 910.6mm2, adj f0,f15,f16,f17,f18,f19,f20,f21
  f23: plane 34x8mm, normal (0,1,0), area 272mm2, adj f4,f15,f22,f24
  f24: plane 34x26mm, normal (-1,0,0), area 566.5mm2, adj f4,f22,f23,f25,f26,f27,f28
  f25: plane 34x8mm, normal (0,-1,0), area 272mm2, adj f4,f15,f22,f24
  f26: plane 25x8mm, normal (0,-1,0), area 200mm2, adj f15,f22,f24,f27
  f27: plane 12.7x8mm, normal (0,0,-1), area 101.6mm2, adj f15,f24,f26,f28
  f28: plane 25x8mm, normal (0,1,0), area 200mm2, adj f15,f22,f24,f27
  f29: cylinder r=1.3mm len=7.2mm, axis (0,0,1), area 58.8mm2, adj f4,f30
  f30: plane 2.6x2.6mm, normal (0,0,1), area 5.3mm2, adj f29
  f31: cylinder r=1.3mm len=7.2mm, axis (0,0,1), area 58.8mm2, adj f4,f32
  f32: plane 2.6x2.6mm, normal (0,0,1), area 5.3mm2, adj f31
  f33: plane 16.02x7.67mm, normal (-0.64,-0.77,0), area 135.6mm2, adj f2,f34,f36,f37,f52
  f34: plane 26x13.07mm, normal (-1,0,0), area 339.8mm2, adj f2,f33,f35,f36
  f35: plane 16.02x7.67mm, normal (-0.64,0.77,0), area 135.6mm2, adj f2,f34,f36,f37,f51
  f36: plane 31.76x6.9mm, normal (0,0,-1), area 173.2mm2, adj f33,f34,f35,f37
  f37: torus R=38.1mm, axis (0,0,-1), area 386.3mm2, adj f0,f33,f35,f36,f51,f52
  f38: cylinder r=1.3mm len=7.2mm, axis (0,0,1), area 58.8mm2, adj f2,f39
  f39: plane 2.6x2.6mm, normal (0,0,1), area 5.3mm2, adj f38
  f40: cylinder r=1.3mm len=7.2mm, axis (0,0,1), area 58.8mm2, adj f2,f41
  f41: plane 2.6x2.6mm, normal (0,0,1), area 5.3mm2, adj f40
  f42: cylinder r=5mm len=10mm, axis (1,0,0), area 120.2mm2, adj f43,f44
  f43: bspline ~12.88x12.54mm, area 71.7mm2, adj f1,f42
  f44: bspline ~12.56x12.2mm, area 65.1mm2, adj f0,f42
  f45: cylinder r=2.54mm len=5.08mm, axis (0,0,-1), area 11.3mm2, adj f3,f17,f18,f22
  f46: cylinder r=2.54mm len=5.08mm, axis (0,0,-1), area 22.3mm2, adj f3,f18,f19,f22
  f47: cylinder r=2.54mm len=5.08mm, axis (0,0,-1), area 22.3mm2, adj f3,f19,f20,f22
  f48: cylinder r=2.54mm len=5.08mm, axis (0,0,1), area 11.3mm2, adj f3,f17,f20,f22
  f49: cylinder r=2.54mm len=5.08mm, axis (0,0,-1), area 21.9mm2, adj f0,f3,f16,f22
  f50: cylinder r=2.54mm len=5.08mm, axis (0,0,-1), area 21.9mm2, adj f0,f3,f21,f22
  f51: cylinder r=1.27mm len=19.42mm, axis (0,0,-1), area 30.7mm2, adj f0,f2,f35,f37
  f52: cylinder r=1.27mm len=19.42mm, axis (0,0,-1), area 30.7mm2, adj f0,f2,f33,f37
PLACE A rot(axis=(-0.92,0.38,0.08),176.1deg) t=(125.99,101.39,129.36)mm
PLACE B rot(axis=(0,0,1),89.9deg) t=(60.04,-286.58,28.88)mm
PLACE C rot(axis=(0.67,0.33,0.67),143.8deg) t=(36.28,-158.15,321.36)mm
PLACE D rot(axis=(0.61,-0.3,-0.73),151.7deg) t=(137.38,96.94,-15.19)mm
PLACE E t=(0.36,0.04,-28.8)mm fixed
MATE parallel B.f8 <-> A.f19  axis (0,0,-1) through (38.46,0.04,28.88)mm
MATE revolute D.f19 <-> B.f23  axis (-1,0,0) through (34.45,-4.16,72.34)mm
MATE revolute D.f15 <-> B.f30  axis (1,0,0) through (20.44,-9.13,38.09)mm
MATE revolute A.f16 <-> E.f31  axis (0,0,1) through (24.71,5.04,10.28)mm
MATE revolute A.f17 <-> E.f29  axis (0,0,-1) through (24.71,-4.96,10.28)mm
MATE revolute D.f19 <-> C.f16  axis (1,0,0) through (36.65,-4.17,72.34)mm
MATE cylindrical B.f8 <-> A.f19  axis (0,0,-1) through (38.46,0.04,28.88)mm
